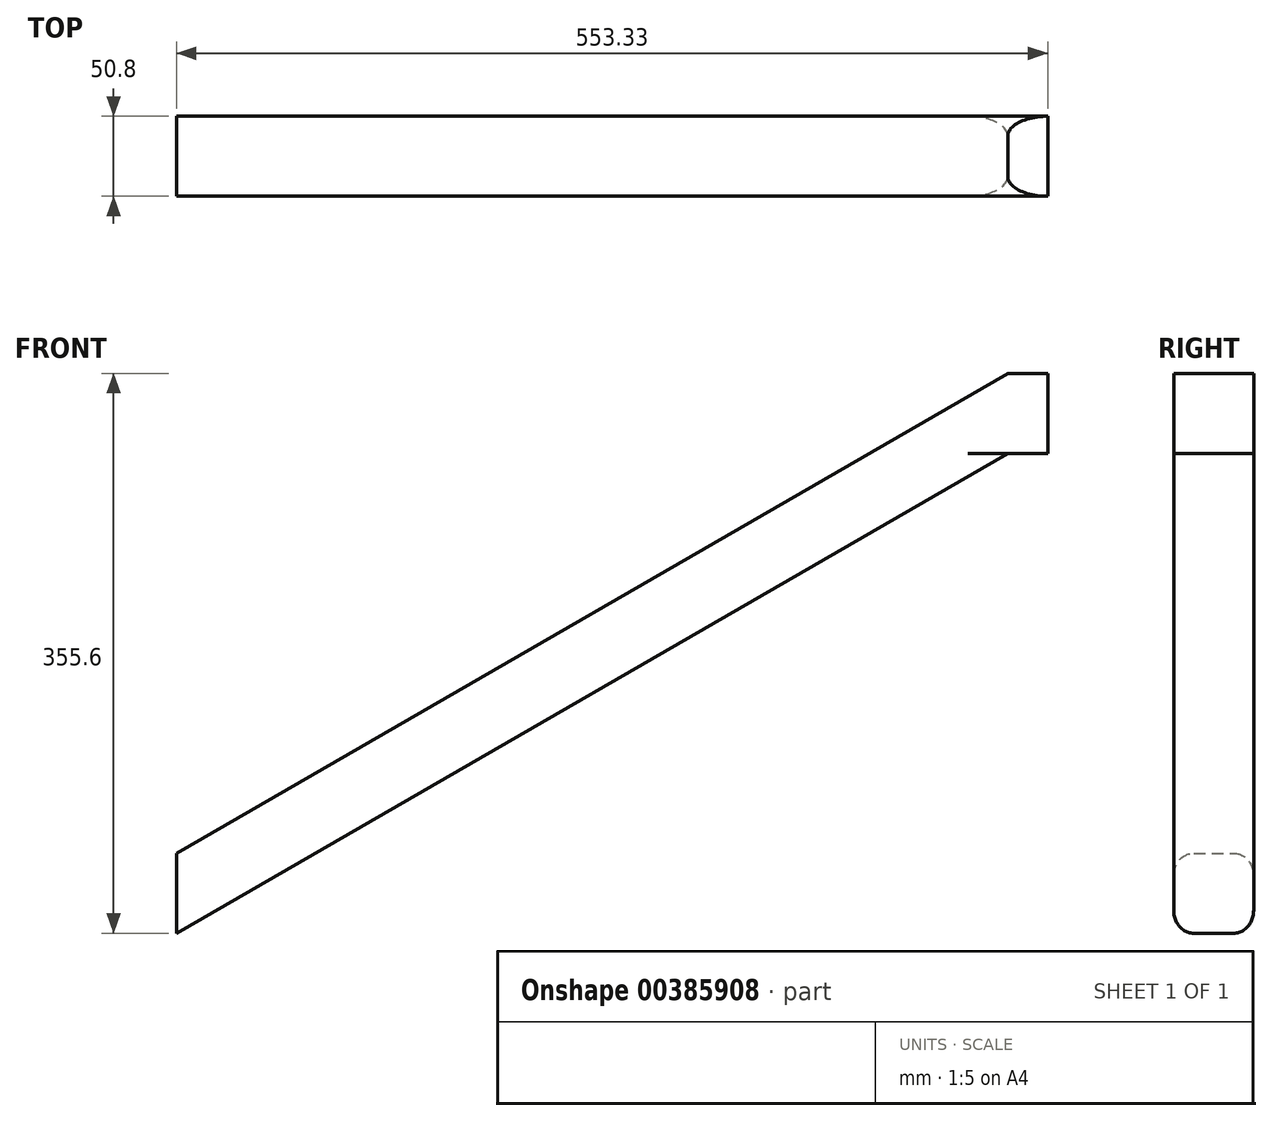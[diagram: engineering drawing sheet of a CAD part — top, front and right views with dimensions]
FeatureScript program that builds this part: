
annotation { "Feature Type Name" : "Feature", "Feature Type Description" : "" }
export const myFeature = defineFeature(function(context is Context, id is Id, definition is map)
    precondition{}
    {
        {
            var Q0;
            Q0=qCreatedBy(makeId("Front.planeOp"),FACE);
            var sketch = newSketch(context, id + "F0", { "sketchPlane" : qUnion([Q0])});
            skLineSegment(sketch, "E0", {"start": v(0, 0) * mm, "end": v(527.93, 304.8) * mm});
            skLineSegment(sketch, "E1", {"start": v(527.93, 304.8) * mm, "end": v(527.93, 254) * mm});
            skLineSegment(sketch, "E2", {"start": v(527.93, 254) * mm, "end": v(0, -50.8) * mm});
            skLineSegment(sketch, "E3", {"start": v(0, -50.8) * mm, "end": v(0, 0) * mm});
            skLineSegment(sketch, "E4.bottom", {"start": v(527.93, 304.8) * mm, "end": v(553.33, 304.8) * mm});
            skLineSegment(sketch, "E4.top", {"start": v(527.93, 254) * mm, "end": v(553.33, 254) * mm});
            skLineSegment(sketch, "E4.right", {"start": v(553.33, 304.8) * mm, "end": v(553.33, 254) * mm});
            skSolve(sketch);
        }
        {
            var Q0;
            Q0 = qSketchRegion(id + "F0", true);
            extrude(context, id + "F1", {"entities" : qUnion([Q0]), "depth" : 50.8 * mm});
        }
        {
            var Q0;
            Q0=makeQuery(id+"F1.opExtrude","CAP_EDGE",EDGE,{"disambiguationData":[OSD([sQuery(id+"F0.wireOp",EDGE,"E0")])],"isStart":false});
            var Q1;
            Q1=makeQuery(id+"F1.opExtrude","CAP_EDGE",EDGE,{"disambiguationData":[OSD([sQuery(id+"F0.wireOp",EDGE,"E2")])],"isStart":false});
            var Q2;
            Q2=makeQuery(id+"F1.opExtrude","CAP_EDGE",EDGE,{"disambiguationData":[OSD([sQuery(id+"F0.wireOp",EDGE,"E0")])],"isStart":true});
            var Q3;
            Q3=makeQuery(id+"F1.opExtrude","CAP_EDGE",EDGE,{"disambiguationData":[OSD([sQuery(id+"F0.wireOp",EDGE,"E2")])],"isStart":true});
            fillet(context, id + "F2", {"entities" : qUnion([Q0, Q1, Q2, Q3]), "radius" : 12.7 * mm, "tangentPropagation" : true, "allowEdgeOverflow" : false});
        }
    });
